# Revit family: Basic PDU
name_source: partatom
category: Installations électriques
units: mm (PartAtom-declared; Revit-internal decimal feet)

## family parameters
Basée sur le plan de construction = Non
Conserver l'orientation des annotations = Non
Cote de connecteur circulaire = Utiliser le diamètre
Couper avec des vides une fois chargée = Non
Numéro OmniClass = 23.80.00.00
Partagée = Non
Point de calcul de pièce = Non
Titre OmniClass = Electric Power and Lighting
Toujours verticalement = Oui
Type d'élément = Normal

## types (13) — shared parameters
Application class = EC002762
BIM wording = Linkeo DATA CENTER BASIC PDU
Color = Black
Connectable by internet box = Non
E-catalogue link = https://www.legrand.fr
Fabricant = LEGRAND
Function = Unit DE DISTRIBUTION D'ENERGIE
IP = IP20
Mounting direction = Vertical
Power frequency = 50-50
Programming way = Non applicable
RAL Number = 9017
Standby consumption = 0 mA
type of voltage = AC
zero-valued in all types: Elévation par défaut

## per-type parameters (varying)
- PDU 0U 3P 16A 36xC13+6xC19: 646910=Oui; 646911=Non; 646960=Non; 646961=Non; 646962=Non; 646963=Non; 646964=Non; 646965=Non; 646971=Non; 646972=Non; 646973=Non; 646974=Non; 646975=Non; Cable cross section MIN_MAX=2.5-2.5; Depth (mm)=67 mm; Description=PDU vertical 3 phase 16A with 36 x C13 + 6 x C19 locking outlets IEC60309; GTIN=3414971972902; Legrand part number=LG-646910; Length=1113 mm; Number of C13 outlets=36; Number of C19 outlets=6; Number of MCB=0; Number of phases=3; Prise_alimentation=Alimentation : Prise rotative; Profondeur cuve + capot=65 mm  [stored 0.213255 ft]; Supply current=16-16; Terminal marking indication=Oui; Type of electric connection=CEE 16 A; Width (mm)=52 mm  [stored 0.170604 ft]
- PDU 0U 3P 16A 24xC13+12xC19: 646910=Non; 646911=Oui; 646960=Non; 646961=Non; 646962=Non; 646963=Non; 646964=Non; 646965=Non; 646971=Non; 646972=Non; 646973=Non; 646974=Non; 646975=Non; Cable cross section MIN_MAX=2.5-2.5; Depth (mm)=67 mm; Description=PDU vertical 3 phase 16A with 24 x C13 + 12 x C19 locking outlets IEC60309; GTIN=3414971972919; Legrand part number=LG-646911; Length=1131 mm; Number of C13 outlets=24; Number of C19 outlets=12; Number of MCB=0; Number of phases=3; Prise_alimentation=Alimentation : Prise rotative; Profondeur cuve + capot=65 mm  [stored 0.213255 ft]; Supply current=16-16; Terminal marking indication=Oui; Type of electric connection=CEE 16 A; Width (mm)=52 mm  [stored 0.170604 ft]
- PDU 0U 1P 16A 18xC13+6xC19: 646910=Non; 646911=Non; 646960=Oui; 646961=Non; 646962=Non; 646963=Non; 646964=Non; 646965=Non; 646971=Non; 646972=Non; 646973=Non; 646974=Non; 646975=Non; Cable cross section MIN_MAX=2.5-2.5; Depth (mm)=60 mm; Description=PDU BASIC 0U 1 PHASE 16A , 18+6 C13/C19 LOCKING OUTLETS , IEC 60309; GTIN=3414972471374; Legrand part number=LG-646960; Length=975 mm  [stored 3.19882 ft]; Number of C13 outlets=18; Number of C19 outlets=6; Number of MCB=0; Number of phases=1; Prise_alimentation=Alimentation : Prise rotative; Profondeur cuve + capot=58 mm; Supply current=16-16; Terminal marking indication=Oui; Type of electric connection=CEE 16 A; Width (mm)=44 mm
- PDU 0U 1P 16A 20xC13+4xC19: 646910=Non; 646911=Non; 646960=Non; 646961=Oui; 646962=Non; 646963=Non; 646964=Non; 646965=Non; 646971=Non; 646972=Non; 646973=Non; 646974=Non; 646975=Non; Cable cross section MIN_MAX=1.5-2.5; Depth (mm)=60 mm; Description=PDU BASIC 0U 1 PHASE 16A , 20+4 C13/C19 LOCKING OUTLETS , IEC-320 C20; GTIN=3414972471381; Legrand part number=LG-646961; Length=902 mm; Number of C13 outlets=20; Number of C19 outlets=4; Number of MCB=0; Number of phases=1; Prise_alimentation=Alimentation : Prise rectangulaire; Profondeur cuve + capot=58 mm; Supply current=16-16; Terminal marking indication=Non; Type of electric connection=C20; Width (mm)=44 mm
- PDU 0U 1P 32A 20xC13+4xC19: 646910=Non; 646911=Non; 646960=Non; 646961=Non; 646962=Oui; 646963=Non; 646964=Non; 646965=Non; 646971=Non; 646972=Non; 646973=Non; 646974=Non; 646975=Non; Cable cross section MIN_MAX=6-6; Depth (mm)=75 mm; Description=PDU BASIC 0U 1 PHASE 32A , 20+4 C13/C19 LOCKING OUTLETS , IEC 60309; GTIN=3414972471398; Legrand part number=LG-646962; Length=1092 mm; Number of C13 outlets=20; Number of C19 outlets=4; Number of MCB=2; Number of phases=1; Prise_alimentation=Alimentation : Prise rotative; Profondeur cuve + capot=58 mm; Supply current=32-32; Terminal marking indication=Oui; Type of electric connection=CEE 32 A; Width (mm)=44 mm
- PDU 0U 1P 32A 12xC13+12xC19: 646910=Non; 646911=Non; 646960=Non; 646961=Non; 646962=Non; 646963=Oui; 646964=Non; 646965=Non; 646971=Non; 646972=Non; 646973=Non; 646974=Non; 646975=Non; Cable cross section MIN_MAX=6-6; Depth (mm)=75 mm; Description=PDU BASIC 0U 1 PHASE 32A , 12+12 C13/C19 LOCKING OUTLETS , IEC 60309; GTIN=3414972471404; Legrand part number=LG-646963; Length=1164 mm; Number of C13 outlets=12; Number of C19 outlets=12; Number of MCB=2; Number of phases=1; Prise_alimentation=Alimentation : Prise rotative; Profondeur cuve + capot=58 mm; Supply current=32-32; Terminal marking indication=Oui; Type of electric connection=CEE 16 A; Width (mm)=44 mm
- PDU 0U 3P 16A 21xC13+3xC19: 646910=Non; 646911=Non; 646960=Non; 646961=Non; 646962=Non; 646963=Non; 646964=Oui; 646965=Non; 646971=Non; 646972=Non; 646973=Non; 646974=Non; 646975=Non; Cable cross section MIN_MAX=2.5-2.5; Depth (mm)=60 mm; Description=PDU BASIC 0U 3 PHASE 16A , 21+3 C13/C19 LOCKING OUTLETS , IEC 60309; GTIN=3414972471411; Legrand part number=LG-646964; Length=978 mm; Number of C13 outlets=21; Number of C19 outlets=3; Number of MCB=0; Number of phases=3; Prise_alimentation=Alimentation : Prise rotative; Profondeur cuve + capot=58 mm; Supply current=16-16; Terminal marking indication=Oui; Type of electric connection=CEE 16 A; Width (mm)=44 mm
- PDU 0U 3P 16A 24xC13+6xC19: 646910=Non; 646911=Non; 646960=Non; 646961=Non; 646962=Non; 646963=Non; 646964=Non; 646965=Oui; 646971=Non; 646972=Non; 646973=Non; 646974=Non; 646975=Non; Cable cross section MIN_MAX=2.5-2.5; Depth (mm)=60 mm; Description=PDU BASIC 0U 3 PHASE 16A , 24+6 C13/C19 LOCKING OUTLETS , IEC 60309; GTIN=3414972471428; Legrand part number=LG-646965; Length=1203 mm; Number of C13 outlets=24; Number of C19 outlets=6; Number of MCB=0; Number of phases=3; Prise_alimentation=Alimentation : Prise rotative; Profondeur cuve + capot=58 mm; Supply current=16-16; Terminal marking indication=Oui; Type of electric connection=CEE 16 A; Width (mm)=44 mm
- PDU HD 0U 1P 32A 24xC13+12xC19: 646910=Non; 646911=Non; 646960=Non; 646961=Non; 646962=Non; 646963=Non; 646964=Non; 646965=Non; 646971=Oui; 646972=Non; 646973=Non; 646974=Non; 646975=Non; Cable cross section MIN_MAX=6-6; Depth (mm)=82 mm; Description=PDU HD BASIC 0U 1 PHASE 32A , 24+12 C13/C19  LOCKING OUTLETS , IEC 60309; GTIN=3414972471459; Legrand part number=LG-646971; Length=1236 mm; Number of C13 outlets=24; Number of C19 outlets=12; Number of MCB=2; Number of phases=1; Prise_alimentation=Alimentation : Prise rotative; Profondeur cuve + capot=65 mm  [stored 0.213255 ft]; Supply current=32-32; Terminal marking indication=Oui; Type of electric connection=CEE 32 A; Width (mm)=52 mm  [stored 0.170604 ft]
- PDU HD 0U 1P 32A 36xC13+6xC19: 646910=Non; 646911=Non; 646960=Non; 646961=Non; 646962=Non; 646963=Non; 646964=Non; 646965=Non; 646971=Non; 646972=Oui; 646973=Non; 646974=Non; 646975=Non; Cable cross section MIN_MAX=6-6; Depth (mm)=82 mm; Description=PDU HD BASIC 0U 1 PHASE 32A , 36+6 C13/C19  LOCKING OUTLETS , IEC 60309; GTIN=3414972471466; Legrand part number=LG-646972; Length=1218 mm; Number of C13 outlets=36; Number of C19 outlets=6; Number of MCB=2; Number of phases=1; Prise_alimentation=Alimentation : Prise rotative; Profondeur cuve + capot=65 mm  [stored 0.213255 ft]; Supply current=32-32; Terminal marking indication=Oui; Type of electric connection=CEE 32 A; Width (mm)=52 mm  [stored 0.170604 ft]
- PDU HD 0U 3P 32A 24xC13+12xC19: 646910=Non; 646911=Non; 646960=Non; 646961=Non; 646962=Non; 646963=Non; 646964=Non; 646965=Non; 646971=Non; 646972=Non; 646973=Oui; 646974=Non; 646975=Non; Cable cross section MIN_MAX=6-6; Depth (mm)=82 mm; Description=PDU HD BASIC 0U 3 PHASE 32A , 24+12 C13/C19 LOCKING OUTLETS, IEC 60309; GTIN=3414972471473; Legrand part number=LG-646973; Length=1506 mm; Number of C13 outlets=24; Number of C19 outlets=12; Number of MCB=6; Number of phases=3; Prise_alimentation=Alimentation : Prise rotative; Profondeur cuve + capot=65 mm  [stored 0.213255 ft]; Supply current=32-32; Terminal marking indication=Oui; Type of electric connection=CEE 32 A; Width (mm)=52 mm  [stored 0.170604 ft]
- PDU HD 0U 3P 32A 36xC13+12xC19: 646910=Non; 646911=Non; 646960=Non; 646961=Non; 646962=Non; 646963=Non; 646964=Non; 646965=Non; 646971=Non; 646972=Non; 646973=Non; 646974=Oui; 646975=Non; Cable cross section MIN_MAX=6-6; Depth (mm)=82 mm; Description=PDU HD BASIC 0U 3 PHASE 32A , 36+12 C13/C19 LOCKING OUTLETS, IEC 60309; GTIN=3414972471480; Legrand part number=LG-646974; Length=1740 mm; Number of C13 outlets=36; Number of C19 outlets=12; Number of MCB=6; Number of phases=3; Prise_alimentation=Alimentation : Prise rotative; Profondeur cuve + capot=65 mm  [stored 0.213255 ft]; Supply current=32-32; Terminal marking indication=Oui; Type of electric connection=CEE 32 A; Width (mm)=52 mm  [stored 0.170604 ft]
- PDU HD 0U 3P 32A 36xC13+6xC19: 646910=Non; 646911=Non; 646960=Non; 646961=Non; 646962=Non; 646963=Non; 646964=Non; 646965=Non; 646971=Non; 646972=Non; 646973=Non; 646974=Non; 646975=Oui; Cable cross section MIN_MAX=6-6; Depth (mm)=82 mm; Description=PDU HD BASIC 0U 3 PHASE 32A , 36+6 C13/C19 LOCKING OUTLETS, IEC 60309; GTIN=3414972471497; Legrand part number=LG-646975; Length=1488 mm  [stored 4.88189 ft]; Number of C13 outlets=36; Number of C19 outlets=6; Number of MCB=6; Number of phases=3; Prise_alimentation=Alimentation : Prise rotative; Profondeur cuve + capot=65 mm  [stored 0.213255 ft]; Supply current=32-32; Terminal marking indication=Oui; Type of electric connection=CEE 32 A; Width (mm)=52 mm  [stored 0.170604 ft]

note: [stored X ft] marks values corroborated as IEEE doubles in the binary element streams (Revit-internal decimal feet)
